AUTODESK INVENTOR PART (.ipt)
format: ipt  version: 2020 (Build 240168000, 168)  size: 115,712 bytes
history: native  units: mm
features: other x19, plane x2
ambient origin geometry x8: Origin, YZ Plane, XZ Plane, XY Plane, X Axis, Y Axis, Z Axis, Center Point
feature tree (21):
  other  "planform"
  plane  "Work Plane8"
  plane  "Work Plane9"
  other  "root_plane_base"
  other  "tip_plane_base"
  other  "UCS_root"
  other  "UCS_tip"
  other  "UCS_root: YZ Plane"
  other  "UCS_root: XZ Plane"
  other  "UCS_root: XY Plane"
  other  "UCS_root: X Axis"
  other  "UCS_root: Y Axis"
  other  "UCS_root: Z Axis"
  other  "UCS_root: Center Point"
  other  "UCS_tip: YZ Plane"
  other  "UCS_tip: XZ Plane"
  other  "UCS_tip: XY Plane"
  other  "UCS_tip: X Axis"
  other  "UCS_tip: Y Axis"
  other  "UCS_tip: Z Axis"
  other  "UCS_tip: Center Point"
